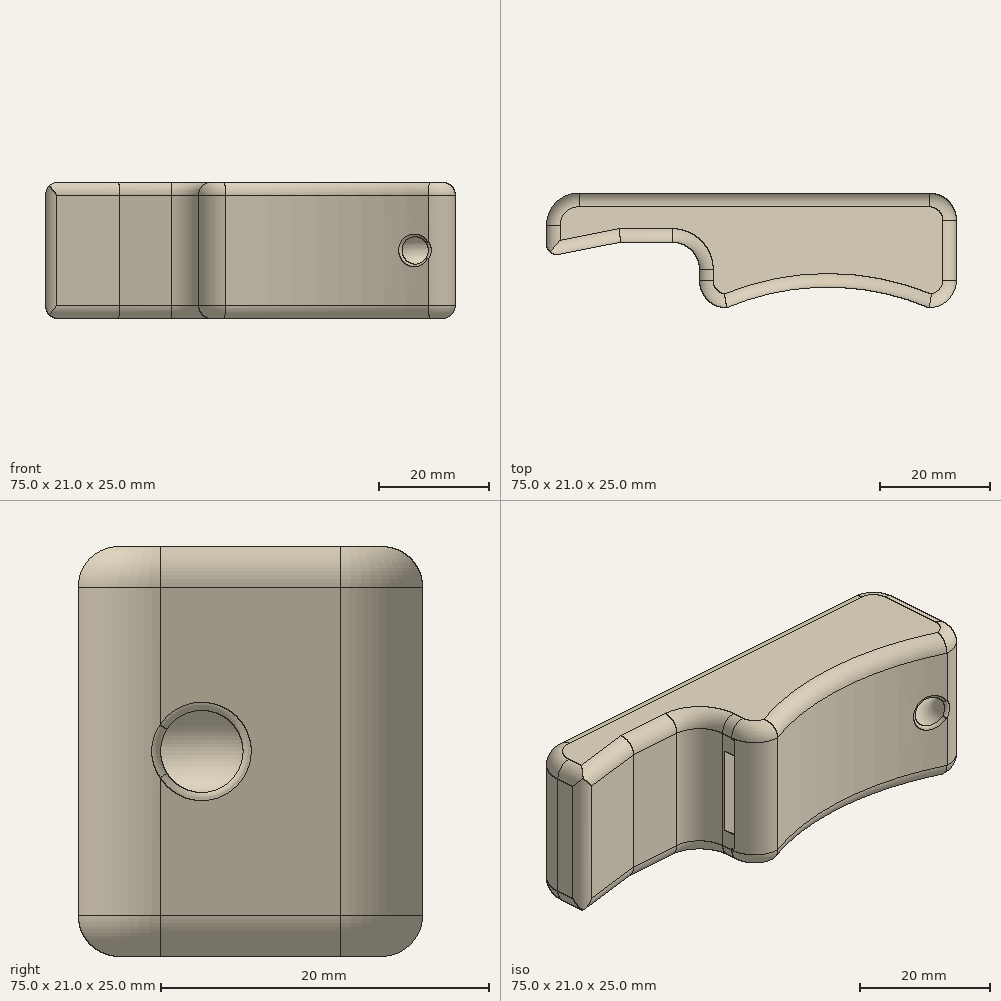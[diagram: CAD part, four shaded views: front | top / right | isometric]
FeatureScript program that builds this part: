
annotation { "Feature Type Name" : "Feature", "Feature Type Description" : "" }
export const myFeature = defineFeature(function(context is Context, id is Id, definition is map)
    precondition{}
    {
        {
            var Q0;
            Q0=qCreatedBy(makeId("Top.planeOp"),FACE);
            var sketch = newSketch(context, id + "F0", { "sketchPlane" : qUnion([Q0])});
            skLineSegment(sketch, "E0", {"start": v(5, -2) * mm, "end": v(5, 0) * mm});
            skPoint(sketch, "E1.visualSharp", {"position": v(0, 0) * mm});
            skArc(sketch, "E1.filletArc", {"start": v(5, 0) * mm, "mid": v(3.54, 3.54) * mm, "end": v(0, 5) * mm});
            skArc(sketch, "E2.filletArc", {"start": v(47, -7) * mm, "mid": v(50.54, -5.54) * mm, "end": v(52, -2) * mm});
            skPoint(sketch, "E3.visualSharp", {"position": v(5, -7) * mm});
            skArc(sketch, "E3.filletArc", {"start": v(5, -2) * mm, "mid": v(6.46, -5.54) * mm, "end": v(10, -7) * mm});
            skLineSegment(sketch, "E4", {"start": v(0, 5) * mm, "end": v(-9.45, 5) * mm});
            skArc(sketch, "E5", {"start": v(-17, 14) * mm, "mid": v(-21.24, 12.24) * mm, "end": v(-23, 8) * mm});
            skLineSegment(sketch, "E6", {"start": v(-23, -19.5) * mm, "end": v(-23, 8) * mm, "construction": true});
            skLineSegment(sketch, "E7", {"start": v(52, -19.5) * mm, "end": v(52, -2) * mm, "construction": true});
            skLineSegment(sketch, "E8", {"start": v(-17, 14) * mm, "end": v(47, 14) * mm});
            skLineSegment(sketch, "E9", {"start": v(52, 9) * mm, "end": v(52, -2) * mm});
            skPoint(sketch, "E10.visualSharp", {"position": v(52, 14) * mm});
            skArc(sketch, "E10.filletArc", {"start": v(52, 9) * mm, "mid": v(50.54, 12.54) * mm, "end": v(47, 14) * mm});
            skArc(sketch, "E11", {"start": v(47, -7) * mm, "mid": v(28.5, -3.21) * mm, "end": v(10, -7) * mm});
            skLineSegment(sketch, "E12", {"start": v(-23, 4.7) * mm, "end": v(-23, 8) * mm});
            skPoint(sketch, "E13.visualSharp", {"position": v(-23, 2.7) * mm});
            skArc(sketch, "E13.filletArc", {"start": v(-23, 4.7) * mm, "mid": v(-22.41, 3.3) * mm, "end": v(-21, 2.7) * mm});
            skLineSegment(sketch, "E14", {"start": v(-21, 2.7) * mm, "end": v(-9.45, 5) * mm});
            skSolve(sketch);
        }
        {
            var Q0;
            Q0=qSketchRegion(id+"F0",true);
            extrude(context, id + "F1", {"entities" : qUnion([Q0]), "endBound" : BoundingType.SYMMETRIC, "depth" : 25 * mm, "offsetDistance" : 25 * mm});
        }
        {
            var Q0;
            Q0=makeQuery(id+"F1.opExtrude","SWEPT_FACE",FACE,{"disambiguationData":[OSD([sQuery(id+"F0.wireOp",EDGE,"E0")])]});
            var sketch = newSketch(context, id + "F2", { "sketchPlane" : qUnion([Q0])});
            skLineSegment(sketch, "E15.bottom", {"start": v(0.5, -9.75) * mm, "end": v(2.5, -9.75) * mm});
            skLineSegment(sketch, "E15.top", {"start": v(0.5, 9.75) * mm, "end": v(2.5, 9.75) * mm});
            skLineSegment(sketch, "E15.left", {"start": v(0.5, -9.75) * mm, "end": v(0.5, 9.75) * mm});
            skLineSegment(sketch, "E15.right", {"start": v(2.5, -9.75) * mm, "end": v(2.5, 9.75) * mm});
            skLineSegment(sketch, "E16", {"start": v(2.5, 12.5) * mm, "end": v(2.5, -12.5) * mm, "construction": true});
            skPoint(sketch, "E17", {"position": v(2.5, 0) * mm});
            skPoint(sketch, "E17.positionSnap0", {"position": v(2.5, 0) * mm});
            skSolve(sketch);
        }
        {
            var Q0;
            Q0=makeQuery(id+"F1.opExtrude","SWEPT_FACE",FACE,{"disambiguationData":[OSD([sQuery(id+"F0.wireOp",EDGE,"E8")])]});
            var sketch = newSketch(context, id + "F3", { "sketchPlane" : qUnion([Q0])});
            skCircle(sketch, "E18", {"center": v(-44.07, 0) * mm, "radius": 3 * mm});
            skPoint(sketch, "E19", {"position": v(-47, 0) * mm});
            skSolve(sketch);
        }
        {
            var Q0;
            Q0=qSketchRegion(id+"F2",true);
            extrude(context, id + "F4", {"entities" : qUnion([Q0]), "operationType" : NewBodyOperationType.REMOVE, "oppositeDirection" : true, "depth" : 16.5 * mm, "offsetDistance" : 25 * mm});
        }
        {
            var Q0;
            Q0=makeQuery(id+"F1.opExtrude","SWEPT_FACE",FACE,{"disambiguationData":[OSD([sQuery(id+"F0.wireOp",EDGE,"E8")])]});
            var sketch = newSketch(context, id + "F5", { "sketchPlane" : qUnion([Q0])});
            skCircle(sketch, "E20", {"center": v(-37.31, 0) * mm, "radius": 1.27 * mm});
            skArc(sketch, "E21", {"start": v(-35.28, 6.05) * mm, "mid": v(-41.7, -4.62) * mm, "end": v(-31.37, 2.34) * mm});
            skArc(sketch, "E22", {"start": v(-37.49, -8.65) * mm, "mid": v(-29.97, -4.58) * mm, "end": v(-29.62, 3.96) * mm});
            skLineSegment(sketch, "E23", {"start": v(-33.52, 7.78) * mm, "end": v(-35.28, 6.05) * mm});
            skLineSegment(sketch, "E24", {"start": v(-29.62, 3.96) * mm, "end": v(-31.37, 2.34) * mm});
            skLineSegment(sketch, "E25", {"start": v(-45.93, -0.75) * mm, "end": v(-45.93, -8.59) * mm});
            skLineSegment(sketch, "E26", {"start": v(-37.49, -8.65) * mm, "end": v(-45.93, -8.59) * mm});
            skArc(sketch, "E27.trimOffspring", {"start": v(-33.52, 7.78) * mm, "mid": v(-42.21, 7.13) * mm, "end": v(-45.93, -0.75) * mm});
            skSolve(sketch);
        }
        {
            var Q0;
            Q0=makeQuery(id+"F5.imprint","IMPRINT",FACE,{"disambiguationData":[TD([[makeQuery(id+"F5.imprint","IMPRINT",EDGE,{"derivedFrom":sQuery(id+"F5.wireOp",EDGE,"E20")}),-1.0]])]});
            var sketch = newSketch(context, id + "F6", { "sketchPlane" : qUnion([Q0])});
            skText(sketch, "E28", { "text": "CORNER", "fontName": "OpenSans-Bold.ttf"});
            skText(sketch, "E29", { "text": "BIKESHOP", "fontName": "OpenSans-Regular.ttf"});
            const initialGuessF6  = {"E28": [-0.02795, 0.00067, 1, 0, 0.00773], "E29": [-0.02795, -0.00678, 1, 0, 0.00678]};
            skSetInitialGuess(sketch, initialGuessF6);
            skSolve(sketch);
        }
        {
            var Q0;
            Q0=makeQuery(id+"F5.imprint","IMPRINT",FACE,{"disambiguationData":[TD([[makeQuery(id+"F5.imprint","IMPRINT",EDGE,{"derivedFrom":sQuery(id+"F5.wireOp",EDGE,"E21")}),-1.0]])]});
            var Q1;
            Q1 = qSketchRegion(id + "F6", true);
            var Q2;
            Q2=makeQuery(id+"F5.imprint","IMPRINT",FACE,{"disambiguationData":[TD([[makeQuery(id+"F5.imprint","IMPRINT",EDGE,{"derivedFrom":sQuery(id+"F5.wireOp",EDGE,"E20")}),1.0]])]});
            extrude(context, id + "F7", {"entities" : qUnion([Q0, Q1, Q2]), "operationType" : NewBodyOperationType.REMOVE, "oppositeDirection" : true, "depth" : 3 * mm, "offsetDistance" : 25 * mm});
        }
        {
            var Q0;
            Q0=makeQuery(id+"F4.boolean.opBoolean","COPY",FACE,{"derivedFrom":makeQuery(id+"F4.opExtrude","SWEPT_FACE",FACE,{"disambiguationData":[OSD([sQuery(id+"F2.wireOp",EDGE,"E15.left")])]})});
            var sketch = newSketch(context, id + "F8", { "sketchPlane" : qUnion([Q0])});
            skPoint(sketch, "E30.first.point", {"position": v(21.5, 0) * mm});
            skPoint(sketch, "E30.second.point.positionSnap0", {"position": v(21.5, 0) * mm});
            skLineSegment(sketch, "E31", {"start": v(5, -9.75) * mm, "end": v(21.5, -9.75) * mm});
            skLineSegment(sketch, "E32", {"start": v(21.5, -9.75) * mm, "end": v(21.5, 9.75) * mm});
            skLineSegment(sketch, "E33", {"start": v(21.5, 9.75) * mm, "end": v(5, 9.75) * mm});
            skLineSegment(sketch, "E34", {"start": v(5, 9.75) * mm, "end": v(5, 7.04) * mm});
            skLineSegment(sketch, "E35", {"start": v(5, -9.75) * mm, "end": v(5, -7.04) * mm});
            skArc(sketch, "E36.trimOffspring", {"start": v(5, -7.04) * mm, "mid": v(21.5, 0) * mm, "end": v(5, 7.04) * mm});
            skSolve(sketch);
        }
        {
            var Q0;
            {var subQ0=sQuery(id+"F8.wireOp",EDGE,"E35");Q0=makeQuery(id+"F8.imprint","IMPRINT",FACE,{"disambiguationData":[TD([[makeQuery(id+"F8.imprint","IMPRINT",EDGE,{"derivedFrom":subQ0}),-1.0]])]});}
            var Q1;
            {var subQ0=sQuery(id+"F8.wireOp",EDGE,"E32");var subQ1=sQuery(id+"F8.wireOp",EDGE,"E31");var subQ2=makeQuery(id+"F8.imprint","INTERSECT",VERTEX,{"derivedFrom":[subQ1,subQ0]});Q1=makeQuery(id+"F8.imprint","IMPRINT",FACE,{"disambiguationData":[TD([[makeQuery(id+"F8.imprint","IMPRINT",EDGE,{"disambiguationData":[TD([[subQ2,-1.0]])],"derivedFrom":subQ1}),-1.0]])]});}
            var Q2;
            {var subQ0=sQuery(id+"F8.wireOp",EDGE,"E33");var subQ1=sQuery(id+"F8.wireOp",EDGE,"E32");var subQ2=makeQuery(id+"F8.imprint","INTERSECT",VERTEX,{"derivedFrom":[subQ1,subQ0]});Q2=makeQuery(id+"F8.imprint","IMPRINT",FACE,{"disambiguationData":[TD([[makeQuery(id+"F8.imprint","IMPRINT",EDGE,{"disambiguationData":[TD([[subQ2,1.0]])],"derivedFrom":subQ1}),1.0]])]});}
            var Q3;
            {var subQ0=sQuery(id+"F8.wireOp",EDGE,"E34");Q3=makeQuery(id+"F8.imprint","IMPRINT",FACE,{"disambiguationData":[TD([[makeQuery(id+"F8.imprint","IMPRINT",EDGE,{"derivedFrom":subQ0}),-1.0]])]});}
            extrude(context, id + "F9", {"entities" : qUnion([Q0, Q1, Q2, Q3]), "operationType" : NewBodyOperationType.ADD, "depth" : 2 * mm, "offsetDistance" : 25 * mm});
        }
        {
            var Q0;
            Q0=makeQuery(id+"F1.opExtrude","SWEPT_FACE",FACE,{"disambiguationData":[OSD([sQuery(id+"F0.wireOp",EDGE,"E9")])]});
            var sketch = newSketch(context, id + "F10", { "sketchPlane" : qUnion([Q0])});
            skCircle(sketch, "E37", {"center": v(0.56, 0) * mm, "radius": 2.5 * mm});
            skLineSegment(sketch, "E38", {"start": v(-6.94, 12.64) * mm, "end": v(-6.94, -12.58) * mm});
            skLineSegment(sketch, "E39", {"start": v(-1.94, 0) * mm, "end": v(-6.94, 0) * mm});
            skSolve(sketch);
        }
        {
            var Q0;
            Q0=makeQuery(id+"F10.imprint","IMPRINT",FACE,{"disambiguationData":[TD([[makeQuery(id+"F10.imprint","IMPRINT",EDGE,{"derivedFrom":sQuery(id+"F10.wireOp",EDGE,"E37")}),1.0]])]});
            var Q1;
            Q1=sQuery(id+"F10.wireOp",EDGE,"E38");
            revolve(context, id + "F11", {"operationType" : NewBodyOperationType.REMOVE, "entities" : qUnion([Q0]), "axis" : qUnion([Q1]), "revolveType" : RevolveType.FULL, "oppositeDirection" : true});
        }
        {
            var Q0;
            Q0=makeQuery(id+"F1.opExtrude","CAP_EDGE",EDGE,{"disambiguationData":[OSD([sQuery(id+"F0.wireOp",EDGE,"E8")])],"isStart":true});
            var Q1;
            Q1=makeQuery(id+"F1.opExtrude","CAP_EDGE",EDGE,{"disambiguationData":[OSD([sQuery(id+"F0.wireOp",EDGE,"E9")])],"isStart":true});
            var Q2;
            Q2=makeQuery(id+"F1.opExtrude","CAP_EDGE",EDGE,{"disambiguationData":[OSD([sQuery(id+"F0.wireOp",EDGE,"E11")])],"isStart":true});
            var Q3;
            Q3=makeQuery(id+"F1.opExtrude","CAP_EDGE",EDGE,{"disambiguationData":[OSD([sQuery(id+"F0.wireOp",EDGE,"E1.filletArc")])],"isStart":true});
            var Q4;
            Q4=makeQuery(id+"F1.opExtrude","CAP_EDGE",EDGE,{"disambiguationData":[OSD([sQuery(id+"F0.wireOp",EDGE,"E4")])],"isStart":true});
            var Q5;
            Q5=makeQuery(id+"F1.opExtrude","CAP_EDGE",EDGE,{"disambiguationData":[OSD([sQuery(id+"F0.wireOp",EDGE,"E14")])],"isStart":true});
            var Q6;
            Q6=makeQuery(id+"F1.opExtrude","CAP_EDGE",EDGE,{"disambiguationData":[OSD([sQuery(id+"F0.wireOp",EDGE,"E12")])],"isStart":true});
            var Q7;
            Q7=makeQuery(id+"F1.opExtrude","CAP_EDGE",EDGE,{"disambiguationData":[OSD([sQuery(id+"F0.wireOp",EDGE,"E5")])],"isStart":true});
            var Q8;
            Q8=makeQuery(id+"F1.opExtrude","CAP_EDGE",EDGE,{"disambiguationData":[OSD([sQuery(id+"F0.wireOp",EDGE,"E0")])],"isStart":true});
            var Q9;
            Q9=makeQuery(id+"F1.opExtrude","CAP_EDGE",EDGE,{"disambiguationData":[OSD([sQuery(id+"F0.wireOp",EDGE,"E3.filletArc")])],"isStart":true});
            var Q10;
            Q10=makeQuery(id+"F1.opExtrude","CAP_EDGE",EDGE,{"disambiguationData":[OSD([sQuery(id+"F0.wireOp",EDGE,"E2.filletArc")])],"isStart":true});
            var Q11;
            Q11=makeQuery(id+"F1.opExtrude","CAP_EDGE",EDGE,{"disambiguationData":[OSD([sQuery(id+"F0.wireOp",EDGE,"E10.filletArc")])],"isStart":true});
            var Q12;
            Q12=makeQuery(id+"F1.opExtrude","CAP_EDGE",EDGE,{"disambiguationData":[OSD([sQuery(id+"F0.wireOp",EDGE,"E9")])],"isStart":false});
            var Q13;
            Q13=makeQuery(id+"F1.opExtrude","CAP_EDGE",EDGE,{"disambiguationData":[OSD([sQuery(id+"F0.wireOp",EDGE,"E11")])],"isStart":false});
            var Q14;
            Q14=makeQuery(id+"F1.opExtrude","CAP_EDGE",EDGE,{"disambiguationData":[OSD([sQuery(id+"F0.wireOp",EDGE,"E2.filletArc")])],"isStart":false});
            var Q15;
            Q15=makeQuery(id+"F1.opExtrude","CAP_EDGE",EDGE,{"disambiguationData":[OSD([sQuery(id+"F0.wireOp",EDGE,"E10.filletArc")])],"isStart":false});
            var Q16;
            Q16=makeQuery(id+"F1.opExtrude","CAP_EDGE",EDGE,{"disambiguationData":[OSD([sQuery(id+"F0.wireOp",EDGE,"E8")])],"isStart":false});
            var Q17;
            Q17=makeQuery(id+"F1.opExtrude","CAP_EDGE",EDGE,{"disambiguationData":[OSD([sQuery(id+"F0.wireOp",EDGE,"E5")])],"isStart":false});
            var Q18;
            Q18=makeQuery(id+"F1.opExtrude","CAP_EDGE",EDGE,{"disambiguationData":[OSD([sQuery(id+"F0.wireOp",EDGE,"E14")])],"isStart":false});
            var Q19;
            Q19=makeQuery(id+"F1.opExtrude","CAP_EDGE",EDGE,{"disambiguationData":[OSD([sQuery(id+"F0.wireOp",EDGE,"E4")])],"isStart":false});
            var Q20;
            Q20=makeQuery(id+"F1.opExtrude","CAP_EDGE",EDGE,{"disambiguationData":[OSD([sQuery(id+"F0.wireOp",EDGE,"E1.filletArc")])],"isStart":false});
            var Q21;
            Q21=makeQuery(id+"F1.opExtrude","CAP_EDGE",EDGE,{"disambiguationData":[OSD([sQuery(id+"F0.wireOp",EDGE,"E3.filletArc")])],"isStart":false});
            var Q22;
            Q22=makeQuery(id+"F1.opExtrude","CAP_EDGE",EDGE,{"disambiguationData":[OSD([sQuery(id+"F0.wireOp",EDGE,"E0")])],"isStart":false});
            var Q23;
            Q23=makeQuery(id+"F1.opExtrude","CAP_EDGE",EDGE,{"disambiguationData":[OSD([sQuery(id+"F0.wireOp",EDGE,"E12")])],"isStart":false});
            fillet(context, id + "F12", {"entities" : qUnion([Q0, Q1, Q2, Q3, Q4, Q5, Q6, Q7, Q8, Q9, Q10, Q11, Q12, Q13, Q14, Q15, Q16, Q17, Q18, Q19, Q20, Q21, Q22, Q23]), "radius" : 2.5 * mm, "allowEdgeOverflow" : false});
        }
        {
            var Q0;
            Q0=makeQuery(id+"F11.boolean.opBoolean","INTERSECT",EDGE,{"derivedFrom":[makeQuery(id+"F1.opExtrude","SWEPT_FACE",FACE,{"disambiguationData":[OSD([sQuery(id+"F0.wireOp",EDGE,"E9")])]}),makeQuery(id+"F11.opRevolve","SWEPT_FACE",FACE,{"disambiguationData":[OSD([sQuery(id+"F10.wireOp",EDGE,"E37")])]})]});
            var Q1;
            Q1=makeQuery(id+"F11.boolean.opBoolean","INTERSECT",EDGE,{"derivedFrom":[makeQuery(id+"F1.opExtrude","SWEPT_FACE",FACE,{"disambiguationData":[OSD([sQuery(id+"F0.wireOp",EDGE,"E11")])]}),makeQuery(id+"F11.opRevolve","SWEPT_FACE",FACE,{"disambiguationData":[OSD([sQuery(id+"F10.wireOp",EDGE,"E37")])]})]});
            var Q2;
            Q2=makeQuery(id+"F11.boolean.opBoolean","INTERSECT",EDGE,{"derivedFrom":[makeQuery(id+"F1.opExtrude","SWEPT_FACE",FACE,{"disambiguationData":[OSD([sQuery(id+"F0.wireOp",EDGE,"E2.filletArc")])]}),makeQuery(id+"F11.opRevolve","SWEPT_FACE",FACE,{"disambiguationData":[OSD([sQuery(id+"F10.wireOp",EDGE,"E37")])]})]});
            var Q3;
            Q3=makeQuery(id+"F11.boolean.opBoolean","COPY",FACE,{"derivedFrom":makeQuery(id+"F11.opRevolve","SWEPT_FACE",FACE,{"disambiguationData":[OSD([sQuery(id+"F10.wireOp",EDGE,"E37")])]})});
            fillet(context, id + "F13", {"entities" : qUnion([Q0, Q1, Q2, Q3]), "radius" : .5 * mm, "tangentPropagation" : true, "allowEdgeOverflow" : false});
        }
    });
